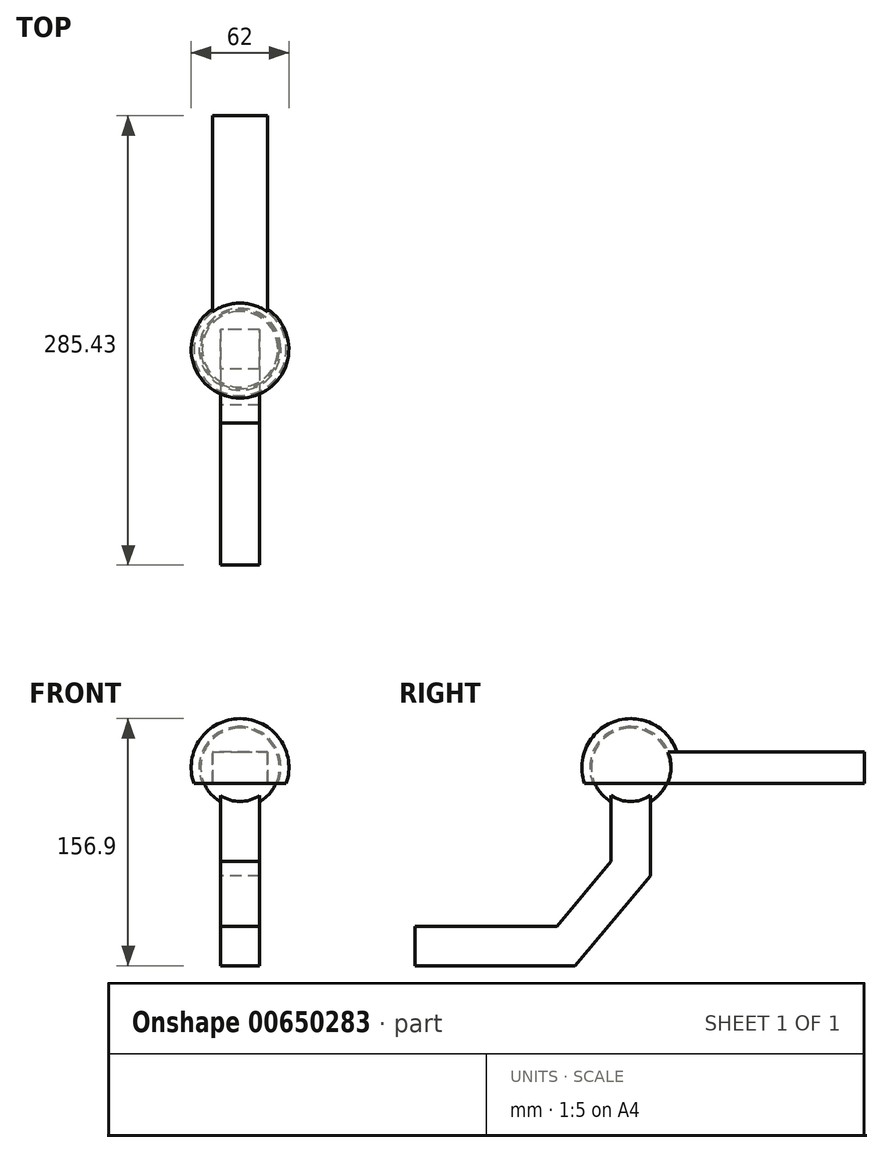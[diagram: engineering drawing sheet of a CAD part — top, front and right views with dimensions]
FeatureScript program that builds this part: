
annotation { "Feature Type Name" : "Feature", "Feature Type Description" : "" }
export const myFeature = defineFeature(function(context is Context, id is Id, definition is map)
    precondition{}
    {
        {
            var Q0;
            Q0=qCreatedBy(makeId("Right.planeOp"),FACE);
            var sketch = newSketch(context, id + "F0", { "sketchPlane" : qUnion([Q0])});
            skCircle(sketch, "E0", {"center": v(0, 0) * mm, "radius": 25 * mm});
            skLineSegment(sketch, "E1", {"start": v(12.5, -21.65) * mm, "end": v(12.5, -68.9) * mm});
            skLineSegment(sketch, "E2", {"start": v(12.5, -68.9) * mm, "end": v(-35.32, -125.9) * mm});
            skLineSegment(sketch, "E3", {"start": v(-35.32, -125.9) * mm, "end": v(-137.13, -125.9) * mm});
            skLineSegment(sketch, "E4", {"start": v(0, 40.88) * mm, "end": v(0, -41.19) * mm, "construction": true});
            skLineSegment(sketch, "E5.0", {"start": v(-46.98, -100.9) * mm, "end": v(-137.13, -100.9) * mm});
            skLineSegment(sketch, "E5.1", {"start": v(-12.5, -59.8) * mm, "end": v(-46.98, -100.9) * mm});
            skLineSegment(sketch, "E5.2", {"start": v(-12.5, -21.65) * mm, "end": v(-12.5, -59.8) * mm});
            skCircle(sketch, "E6.0", {"center": v(0, 0) * mm, "radius": 26 * mm});
            skCircle(sketch, "E7.0", {"center": v(0, 0) * mm, "radius": 31 * mm});
            skLineSegment(sketch, "E8", {"start": v(24, -10) * mm, "end": v(29.34, -10) * mm});
            skLineSegment(sketch, "E9", {"start": v(-137.13, -100.9) * mm, "end": v(-137.13, -125.9) * mm});
            skLineSegment(sketch, "E10", {"start": v(0, 31) * mm, "end": v(0, -31) * mm});
            skLineSegment(sketch, "E11", {"start": v(-12.5, -21.65) * mm, "end": v(-12.5, -9.03) * mm});
            skLineSegment(sketch, "E12", {"start": v(-12.5, -9.03) * mm, "end": v(12.5, -9.03) * mm});
            skLineSegment(sketch, "E13", {"start": v(12.5, -9.03) * mm, "end": v(12.5, -21.65) * mm});
            skSolve(sketch);
        }
        {
            var Q0;
            {var subQ0=sQuery(id+"F0.wireOp",EDGE,"E0");var subQ1=makeQuery(id+"F0.imprint","INTERSECT",VERTEX,{"derivedFrom":[subQ0,sQuery(id+"F0.wireOp",EDGE,"E5.2")]});Q0=makeQuery(id+"F0.imprint","IMPRINT",FACE,{"disambiguationData":[TD([[makeQuery(id+"F0.imprint","IMPRINT",EDGE,{"disambiguationData":[TD([[subQ1,1.0]])],"derivedFrom":subQ0}),1.0]])]});}
            var Q1;
            {var subQ0=sQuery(id+"F0.wireOp",EDGE,"E11");Q1=makeQuery(id+"F0.imprint","IMPRINT",FACE,{"disambiguationData":[TD([[makeQuery(id+"F0.imprint","IMPRINT",EDGE,{"derivedFrom":subQ0}),-1.0]])]});}
            var Q2;
            Q2=sQuery(id+"F0.wireOp",EDGE,"E10");
            revolve(context, id + "F1", {"entities" : qUnion([Q0, Q1]), "axis" : qUnion([Q2]), "revolveType" : RevolveType.FULL});
        }
        {
            var Q0;
            {var subQ4=sQuery(id+"F0.wireOp",EDGE,"E2");Q0=makeQuery(id+"F0.imprint","IMPRINT",FACE,{"disambiguationData":[TD([[makeQuery(id+"F0.imprint","IMPRINT",EDGE,{"derivedFrom":subQ4}),-1.0]])]});}
            var Q1;
            {var subQ0=sQuery(id+"F0.wireOp",EDGE,"E7.0");var subQ1=sQuery(id+"F0.wireOp",EDGE,"E1");var subQ2=makeQuery(id+"F0.imprint","INTERSECT",VERTEX,{"derivedFrom":[subQ1,subQ0]});Q1=makeQuery(id+"F0.imprint","IMPRINT",FACE,{"disambiguationData":[TD([[makeQuery(id+"F0.imprint","IMPRINT",EDGE,{"disambiguationData":[TD([[subQ2,1.0]])],"derivedFrom":subQ1}),-1.0]])]});}
            var Q2;
            {var subQ0=sQuery(id+"F0.wireOp",EDGE,"E7.0");var subQ1=sQuery(id+"F0.wireOp",EDGE,"E5.2");var subQ2=makeQuery(id+"F0.imprint","INTERSECT",VERTEX,{"derivedFrom":[subQ1,subQ0]});Q2=makeQuery(id+"F0.imprint","IMPRINT",FACE,{"disambiguationData":[TD([[makeQuery(id+"F0.imprint","IMPRINT",EDGE,{"disambiguationData":[TD([[subQ2,1.0]])],"derivedFrom":subQ1}),1.0]])]});}
            var Q3;
            {var subQ0=sQuery(id+"F0.wireOp",EDGE,"E5.2");var subQ5=sQuery(id+"F0.wireOp",EDGE,"E6.0");var subQ6=makeQuery(id+"F0.imprint","INTERSECT",VERTEX,{"derivedFrom":[subQ0,subQ5]});Q3=makeQuery(id+"F0.imprint","IMPRINT",FACE,{"disambiguationData":[TD([[makeQuery(id+"F0.imprint","IMPRINT",EDGE,{"disambiguationData":[TD([[subQ6,-1.0]])],"derivedFrom":subQ5}),1.0]])]});}
            var Q4;
            {var subQ0=sQuery(id+"F0.wireOp",EDGE,"E11");Q4=makeQuery(id+"F0.imprint","IMPRINT",FACE,{"disambiguationData":[TD([[makeQuery(id+"F0.imprint","IMPRINT",EDGE,{"derivedFrom":subQ0}),-1.0]])]});}
            var Q5;
            {var subQ0=sQuery(id+"F0.wireOp",EDGE,"E13");Q5=makeQuery(id+"F0.imprint","IMPRINT",FACE,{"disambiguationData":[TD([[makeQuery(id+"F0.imprint","IMPRINT",EDGE,{"derivedFrom":subQ0}),-1.0]])]});}
            var Q6;
            {var subQ0=sQuery(id+"F0.wireOp",EDGE,"E1");var subQ5=sQuery(id+"F0.wireOp",EDGE,"E6.0");var subQ6=makeQuery(id+"F0.imprint","INTERSECT",VERTEX,{"derivedFrom":[subQ0,subQ5]});Q6=makeQuery(id+"F0.imprint","IMPRINT",FACE,{"disambiguationData":[TD([[makeQuery(id+"F0.imprint","IMPRINT",EDGE,{"disambiguationData":[TD([[subQ6,1.0]])],"derivedFrom":subQ5}),1.0]])]});}
            extrude(context, id + "F2", {"entities" : qUnion([Q0, Q1, Q2, Q3, Q4, Q5, Q6]), "operationType" : NewBodyOperationType.ADD, "endBound" : BoundingType.SYMMETRIC, "depth" : 25 * mm, "offsetDistance" : 25 * mm});
        }
        {
            var Q0;
            {var subQ0=sQuery(id+"F0.wireOp",EDGE,"E8");Q0=makeQuery(id+"F0.imprint","IMPRINT",FACE,{"disambiguationData":[TD([[makeQuery(id+"F0.imprint","IMPRINT",EDGE,{"derivedFrom":subQ0}),1.0]])]});}
            var Q1;
            Q1=sQuery(id+"F0.wireOp",EDGE,"E10");
            revolve(context, id + "F3", {"entities" : qUnion([Q0]), "axis" : qUnion([Q1]), "revolveType" : RevolveType.FULL});
        }
        {
            var Q0;
            Q0=qCreatedBy(makeId("Front.planeOp"),FACE);
            cPlane(context, id + "F4", {"entities" : qUnion([Q0]), "cplaneType" : CPlaneType.OFFSET, "offset" : 148.3 * mm, "oppositeDirection" : true, "width" : 150 * mm, "height" : 150 * mm});
        }
        {
            var Q0;
            Q0=qCreatedBy(id+"F4.planeOp",FACE);
            var sketch = newSketch(context, id + "F5", { "sketchPlane" : qUnion([Q0])});
            skLineSegment(sketch, "E14.0", {"start": v(-29.34, -10) * mm, "end": v(29.34, -10) * mm});
            skLineSegment(sketch, "E15", {"start": v(0, 38.73) * mm, "end": v(0, -15.35) * mm, "construction": true});
            skLineSegment(sketch, "E16", {"start": v(17.5, -10) * mm, "end": v(17.5, 9.9) * mm});
            skLineSegment(sketch, "E17.MirrorCS", {"start": v(-17.5, -10) * mm, "end": v(-17.5, 9.9) * mm});
            skLineSegment(sketch, "E18", {"start": v(17.5, 9.9) * mm, "end": v(-17.5, 9.9) * mm});
            skSolve(sketch);
        }
        {
            var Q0;
            {var subQ0=sQuery(id+"F5.wireOp",EDGE,"E16");Q0=makeQuery(id+"F5.imprint","IMPRINT",FACE,{"disambiguationData":[TD([[makeQuery(id+"F5.imprint","IMPRINT",EDGE,{"derivedFrom":subQ0}),1.0]])]});}
            extrude(context, id + "F6", {"entities" : qUnion([Q0]), "operationType" : NewBodyOperationType.ADD, "endBound" : BoundingType.UP_TO_NEXT, "depth" : 25 * mm, "offsetDistance" : 25 * mm});
        }
    });
